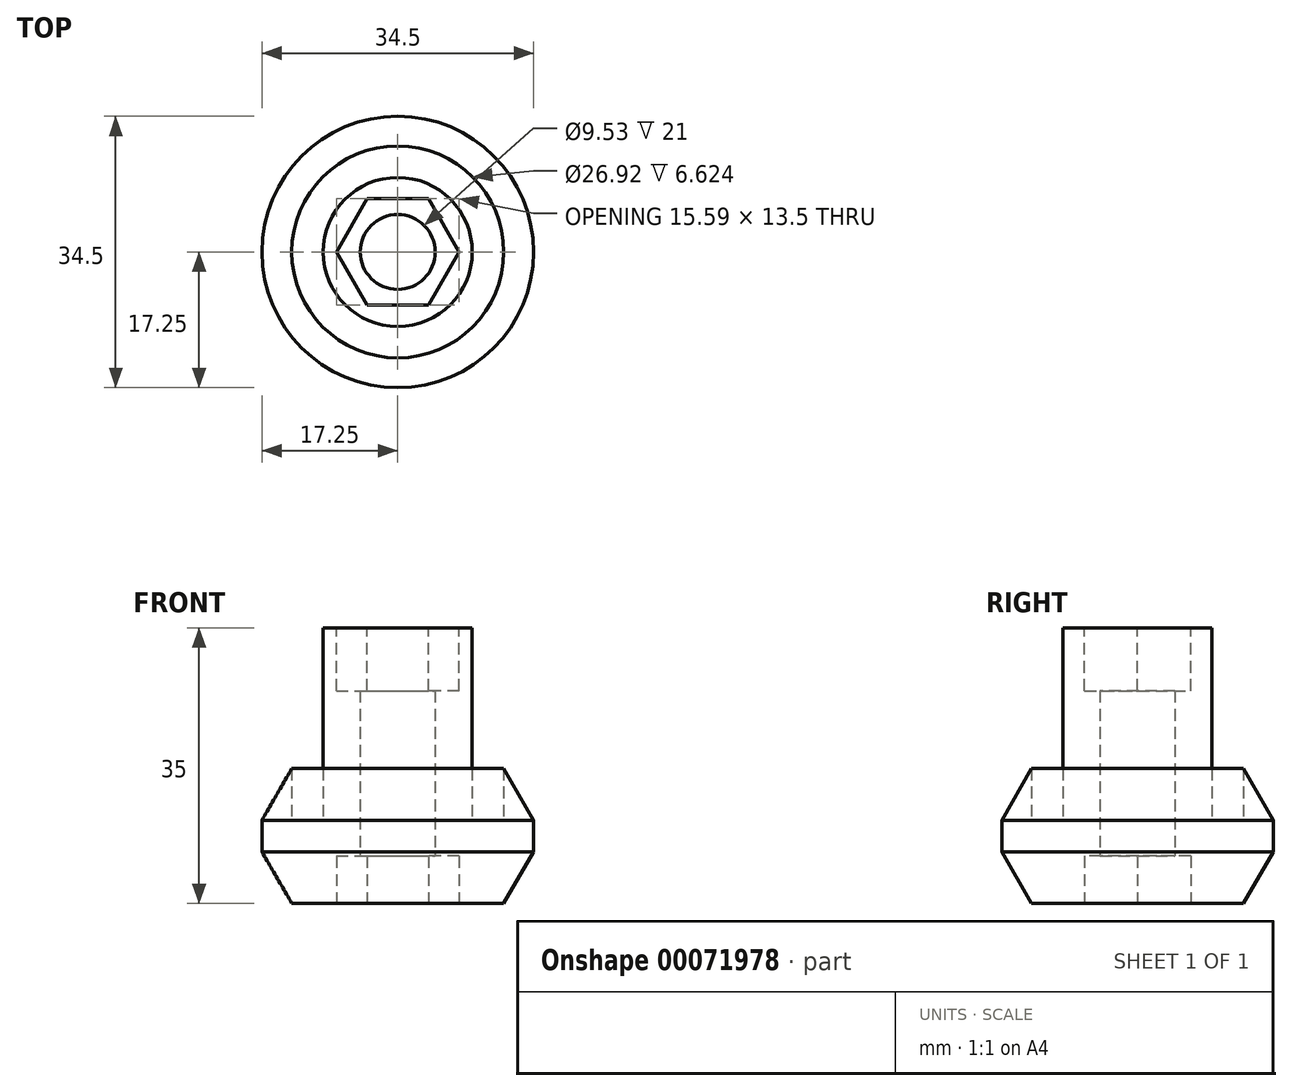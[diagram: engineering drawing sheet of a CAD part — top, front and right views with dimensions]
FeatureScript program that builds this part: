
annotation { "Feature Type Name" : "Feature", "Feature Type Description" : "" }
export const myFeature = defineFeature(function(context is Context, id is Id, definition is map)
    precondition{}
    {
        {
            var Q0;
            Q0=qCreatedBy(makeId("Front.planeOp"),FACE);
            var sketch = newSketch(context, id + "F0", { "sketchPlane" : qUnion([Q0])});
            skLineSegment(sketch, "E0", {"start": v(0, 0) * mm, "end": v(0, 54.65) * mm, "construction": true});
            skLineSegment(sketch, "E1", {"start": v(-4.76, 0) * mm, "end": v(-4.76, 35) * mm});
            skLineSegment(sketch, "E2", {"start": v(-4.76, 0) * mm, "end": v(-13.46, 0) * mm});
            skLineSegment(sketch, "E3", {"start": v(-13.46, 0) * mm, "end": v(-17.25, 6.56) * mm});
            skLineSegment(sketch, "E4", {"start": v(-17.25, 6.56) * mm, "end": v(-17.25, 10.56) * mm});
            skLineSegment(sketch, "E5", {"start": v(-17.25, 10.56) * mm, "end": v(-13.46, 17.12) * mm});
            skLineSegment(sketch, "E6", {"start": v(-13.46, 17.12) * mm, "end": v(-13.46, 10.5) * mm});
            skLineSegment(sketch, "E7", {"start": v(-4.76, 35) * mm, "end": v(-9.46, 35) * mm});
            skLineSegment(sketch, "E8", {"start": v(-9.46, 10.5) * mm, "end": v(-9.46, 35) * mm});
            skLineSegment(sketch, "E9", {"start": v(-9.46, 35) * mm, "end": v(-9.46, 10.5) * mm});
            skLineSegment(sketch, "E10", {"start": v(-9.46, 10.5) * mm, "end": v(-13.46, 10.5) * mm});
            skSolve(sketch);
        }
        {
            var Q0;
            Q0=makeQuery(id+"F0.imprint","IMPRINT",FACE,{"disambiguationData":[TD([[makeQuery(id+"F0.imprint","IMPRINT",EDGE,{"derivedFrom":sQuery(id+"F0.wireOp",EDGE,"E1")}),1.0]])]});
            var Q1;
            Q1=sQuery(id+"F0.wireOp",EDGE,"E0");
            revolve(context, id + "F1", {"entities" : qUnion([Q0]), "axis" : qUnion([Q1]), "revolveType" : RevolveType.FULL});
        }
        {
            var Q0;
            Q0=makeQuery(id+"F1.opRevolve","SWEPT_FACE",FACE,{"disambiguationData":[OSD([sQuery(id+"F0.wireOp",EDGE,"E7")])]});
            var sketch = newSketch(context, id + "F2", { "sketchPlane" : qUnion([Q0])});
            skCircle(sketch, "E11.cCircle", {"center": v(0, 0) * mm, "radius": 6.75 * mm, "construction": true});
            skLineSegment(sketch, "E11.0", {"start": v(-3.9, 6.75) * mm, "end": v(3.9, 6.75) * mm});
            skLineSegment(sketch, "E11.1", {"start": v(3.9, 6.75) * mm, "end": v(7.8, 0) * mm});
            skLineSegment(sketch, "E11.2", {"start": v(7.8, 0) * mm, "end": v(3.9, -6.75) * mm});
            skLineSegment(sketch, "E11.3", {"start": v(3.9, -6.75) * mm, "end": v(-3.9, -6.75) * mm});
            skLineSegment(sketch, "E11.4", {"start": v(-3.9, -6.75) * mm, "end": v(-7.8, 0) * mm});
            skLineSegment(sketch, "E11.5", {"start": v(-7.8, 0) * mm, "end": v(-3.9, 6.75) * mm});
            skPoint(sketch, "E11.0.midPoint", {"position": v(0, 6.75) * mm});
            skSolve(sketch);
        }
        {
            var Q0;
            Q0=makeQuery(id+"F2.imprint","IMPRINT",FACE,{"disambiguationData":[TD([[makeQuery(id+"F2.imprint","IMPRINT",EDGE,{"derivedFrom":sQuery(id+"F2.wireOp",EDGE,"E11.0")}),-1.0]])]});
            extrude(context, id + "F3", {"entities" : qUnion([Q0]), "operationType" : NewBodyOperationType.REMOVE, "oppositeDirection" : true, "depth" : 8 * mm});
        }
        {
            var Q0;
            Q0=makeQuery(id+"F1.opRevolve","SWEPT_FACE",FACE,{"disambiguationData":[OSD([sQuery(id+"F0.wireOp",EDGE,"E2")])]});
            var sketch = newSketch(context, id + "F4", { "sketchPlane" : qUnion([Q0])});
            skCircle(sketch, "E12.cCircle", {"center": v(0, 0) * mm, "radius": 6.75 * mm, "construction": true});
            skLineSegment(sketch, "E12.0", {"start": v(-3.9, 6.75) * mm, "end": v(3.9, 6.75) * mm});
            skLineSegment(sketch, "E12.1", {"start": v(3.9, 6.75) * mm, "end": v(7.8, 0) * mm});
            skLineSegment(sketch, "E12.2", {"start": v(7.8, 0) * mm, "end": v(3.9, -6.75) * mm});
            skLineSegment(sketch, "E12.3", {"start": v(3.9, -6.75) * mm, "end": v(-3.9, -6.75) * mm});
            skLineSegment(sketch, "E12.4", {"start": v(-3.9, -6.75) * mm, "end": v(-7.8, 0) * mm});
            skLineSegment(sketch, "E12.5", {"start": v(-7.8, 0) * mm, "end": v(-3.9, 6.75) * mm});
            skPoint(sketch, "E12.0.midPoint", {"position": v(0, 6.75) * mm});
            skSolve(sketch);
        }
        {
            var Q0;
            Q0=makeQuery(id+"F4.imprint","IMPRINT",FACE,{"disambiguationData":[TD([[makeQuery(id+"F4.imprint","IMPRINT",EDGE,{"derivedFrom":sQuery(id+"F4.wireOp",EDGE,"E12.0")}),-1.0]])]});
            extrude(context, id + "F5", {"entities" : qUnion([Q0]), "operationType" : NewBodyOperationType.REMOVE, "oppositeDirection" : true, "depth" : 6 * mm});
        }
    });
